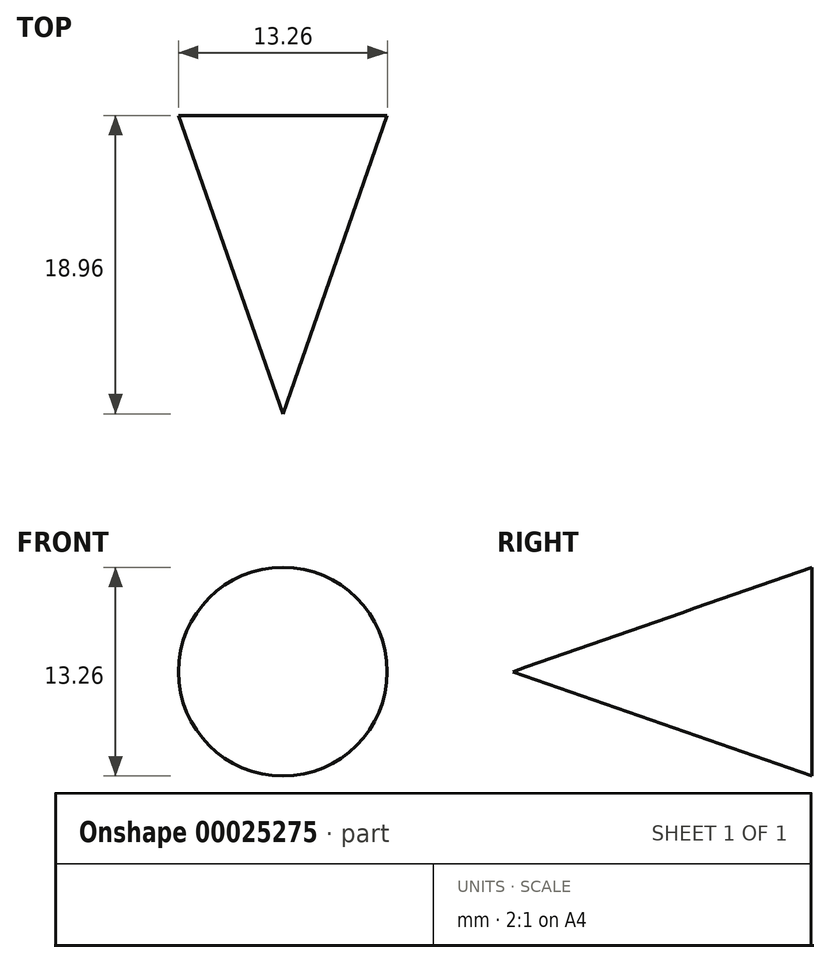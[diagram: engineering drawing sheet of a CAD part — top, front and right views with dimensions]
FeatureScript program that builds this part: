
annotation { "Feature Type Name" : "Feature", "Feature Type Description" : "" }
export const myFeature = defineFeature(function(context is Context, id is Id, definition is map)
    precondition{}
    {
        {
            var Q0;
            Q0=qCreatedBy(makeId("Right.planeOp"),FACE);
            var sketch = newSketch(context, id + "F0", { "sketchPlane" : qUnion([Q0])});
            skLineSegment(sketch, "E0", {"start": v(0, 36.02) * mm, "end": v(-18.96, 36.02) * mm});
            skLineSegment(sketch, "E1", {"start": v(-18.96, 36.02) * mm, "end": v(0, 42.65) * mm});
            skLineSegment(sketch, "E2", {"start": v(0, 42.65) * mm, "end": v(0, 36.02) * mm});
            skLineSegment(sketch, "E3", {"start": v(-18.96, 36.02) * mm, "end": v(0, 28.82) * mm});
            skLineSegment(sketch, "E4", {"start": v(0, 36.02) * mm, "end": v(0, 28.82) * mm});
            skSolve(sketch);
        }
        {
            var Q0;
            Q0=makeQuery(id+"F0.imprint","IMPRINT",FACE,{"disambiguationData":[TD([[makeQuery(id+"F0.imprint","IMPRINT",EDGE,{"derivedFrom":sQuery(id+"F0.wireOp",EDGE,"E0")}),-1.0]])]});
            var Q1;
            Q1=sQuery(id+"F0.wireOp",EDGE,"E0");
            revolve(context, id + "F1", {"entities" : qUnion([Q0]), "axis" : qUnion([Q1]), "revolveType" : RevolveType.FULL});
        }
    });
